# Revit family: LXEW
name_source: partatom
category: Lighting Fixtures
units: mm (PartAtom-declared; Revit-internal decimal feet)

## family parameters
Cut with Voids When Loaded = No
Host = Face
Light Source = Yes
OmniClass Number = 23.80.70.11
OmniClass Title = Luminaries for Internal Lighting
Part Type = Normal
Room Calculation Point = No
Round Connector Dimension = Use Diameter
Shared = Yes

## types (2) — shared parameters
Apparent Load = 0 VA
Backbox = White
Color Filter = 16777215
Default Elevation = 4.00'
Description = LXEW Wide-Body Enclosed and Gasketed is as practical as it is flexible with high efficacy LED for low maintenance and energy savings
Dimming Lamp Color Temperature Shift = <None>
Driver = Fixed Output
Emit from Line Length = 2.00'
Glass = White Glass
Lamp = LED Lamp
Lens = Frost Impact Resistant Acrylic (std.)
Lumen Output = High Lumen
Manufacturer = Columbia Lighting
Model = LXEW
Nominal Watts = 225 W
Row Length = 4.00'
Tilt Angle = -90.00°
URL = https://www.currentlighting.com
Voltage = 120 V

## per-type parameters (varying)
| type | Distribution | Photometric Web File |
| LXEW4-40H-N-FA-EU | Narrow Distribution | LXEW4-40H-N-FA-EU.ies |
| LXEW4-40H-W-FA-EU | Wide Distribution | LXEW4-40H-W-FA-EU.ies |

## geometry (parser evidence)
native form markers: Sweep x3
no freeform markers — native parametric forms only
